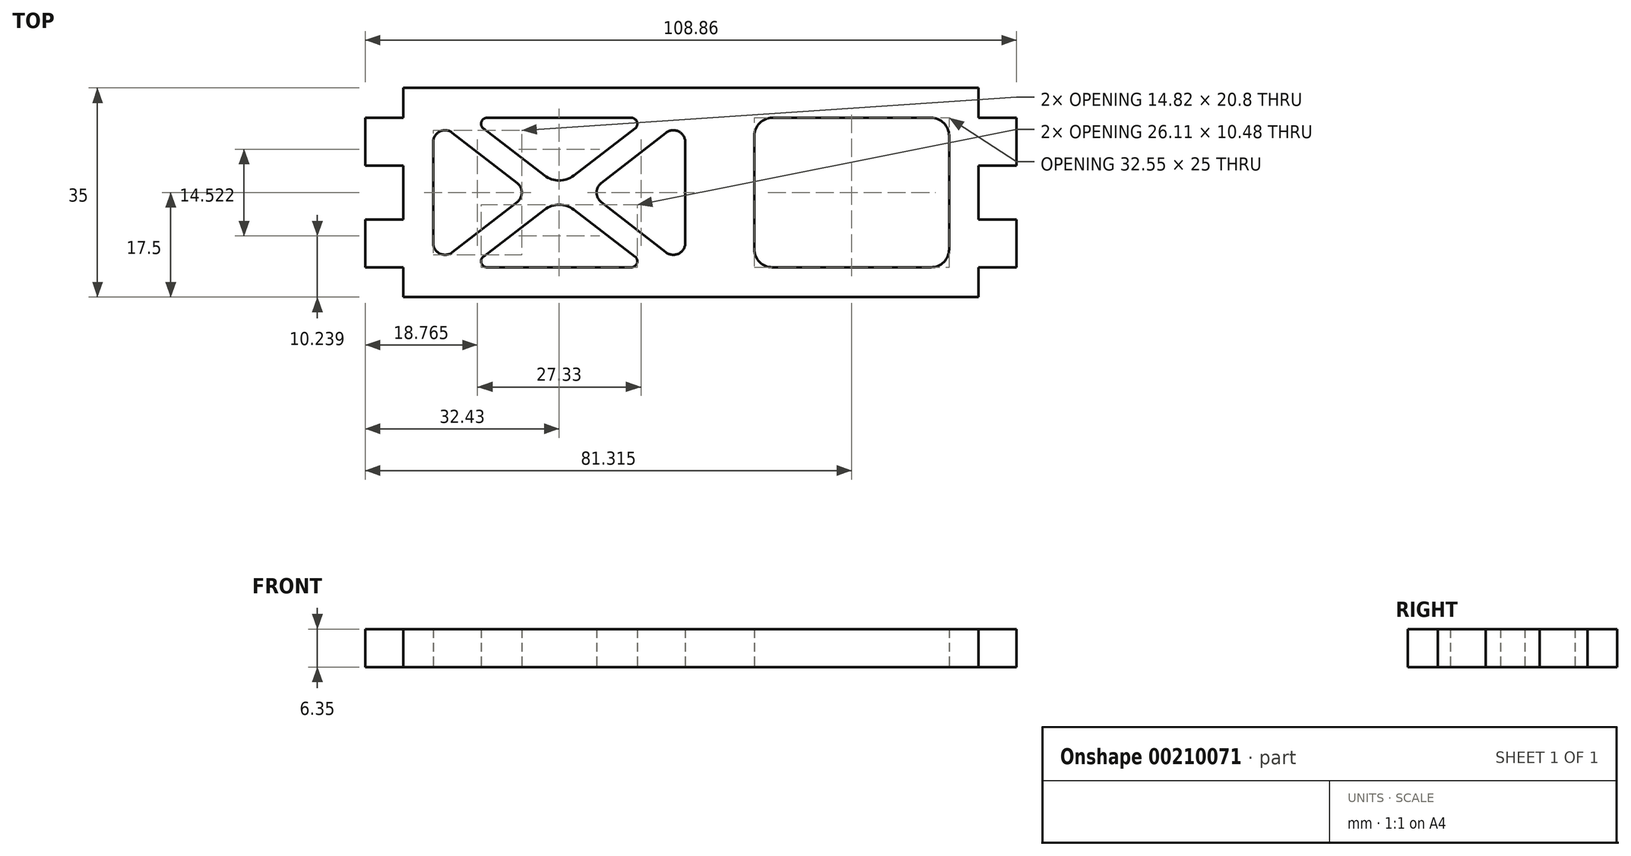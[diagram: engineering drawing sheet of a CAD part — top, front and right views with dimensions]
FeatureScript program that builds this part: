
annotation { "Feature Type Name" : "Feature", "Feature Type Description" : "" }
export const myFeature = defineFeature(function(context is Context, id is Id, definition is map)
    precondition{}
    {
        {
            var Q0;
            Q0=qCreatedBy(makeId("Top.planeOp"),FACE);
            var sketch = newSketch(context, id + "F0", { "sketchPlane" : qUnion([Q0])});
            skLineSegment(sketch, "E0.bottom", {"start": v(-48.08, 17.5) * mm, "end": v(48.08, 17.5) * mm});
            skLineSegment(sketch, "E0.top", {"start": v(-48.08, -17.5) * mm, "end": v(48.08, -17.5) * mm});
            skLineSegment(sketch, "E0.left", {"start": v(-48.08, 17.5) * mm, "end": v(-48.08, -17.5) * mm});
            skLineSegment(sketch, "E0.right", {"start": v(48.08, 17.5) * mm, "end": v(48.08, -17.5) * mm});
            skPoint(sketch, "E0.middle", {"position": v(0, 0) * mm});
            skLineSegment(sketch, "E1.bottom", {"start": v(48.08, 12.5) * mm, "end": v(54.43, 12.5) * mm});
            skLineSegment(sketch, "E1.top", {"start": v(48.08, 4.5) * mm, "end": v(54.43, 4.5) * mm});
            skLineSegment(sketch, "E1.left", {"start": v(48.08, 12.5) * mm, "end": v(48.08, 4.5) * mm});
            skLineSegment(sketch, "E1.right", {"start": v(54.43, 12.5) * mm, "end": v(54.43, 4.5) * mm});
            skLineSegment(sketch, "E2.bottom", {"start": v(48.08, -4.5) * mm, "end": v(54.43, -4.5) * mm});
            skLineSegment(sketch, "E2.top", {"start": v(48.08, -12.5) * mm, "end": v(54.43, -12.5) * mm});
            skLineSegment(sketch, "E2.left", {"start": v(48.08, -4.5) * mm, "end": v(48.08, -12.5) * mm});
            skLineSegment(sketch, "E2.right", {"start": v(54.43, -4.5) * mm, "end": v(54.43, -12.5) * mm});
            skLineSegment(sketch, "E3.bottom", {"start": v(-48.08, 12.5) * mm, "end": v(-54.43, 12.5) * mm});
            skLineSegment(sketch, "E3.top", {"start": v(-48.08, 4.5) * mm, "end": v(-54.43, 4.5) * mm});
            skLineSegment(sketch, "E3.left", {"start": v(-48.08, 12.5) * mm, "end": v(-48.08, 4.5) * mm});
            skLineSegment(sketch, "E3.right", {"start": v(-54.43, 12.5) * mm, "end": v(-54.43, 4.5) * mm});
            skLineSegment(sketch, "E4.bottom", {"start": v(-48.08, -4.5) * mm, "end": v(-54.43, -4.5) * mm});
            skLineSegment(sketch, "E4.top", {"start": v(-48.08, -12.5) * mm, "end": v(-54.43, -12.5) * mm});
            skLineSegment(sketch, "E4.left", {"start": v(-48.08, -4.5) * mm, "end": v(-48.08, -12.5) * mm});
            skLineSegment(sketch, "E4.right", {"start": v(-54.43, -4.5) * mm, "end": v(-54.43, -12.5) * mm});
            skLineSegment(sketch, "E5.bottom", {"start": v(-33.75, -17.5) * mm, "end": v(-22.5, -17.5) * mm});
            skLineSegment(sketch, "E5.top", {"start": v(-33.75, -23.85) * mm, "end": v(-22.5, -23.85) * mm});
            skLineSegment(sketch, "E5.left", {"start": v(-33.75, -17.5) * mm, "end": v(-33.75, -23.85) * mm});
            skLineSegment(sketch, "E5.right", {"start": v(-22.5, -17.5) * mm, "end": v(-22.5, -23.85) * mm});
            skLineSegment(sketch, "E6.bottom", {"start": v(-2.5, -17.5) * mm, "end": v(8.75, -17.5) * mm});
            skLineSegment(sketch, "E6.top", {"start": v(-2.5, -23.85) * mm, "end": v(8.75, -23.85) * mm});
            skLineSegment(sketch, "E6.left", {"start": v(-2.5, -17.5) * mm, "end": v(-2.5, -23.85) * mm});
            skLineSegment(sketch, "E6.right", {"start": v(8.75, -17.5) * mm, "end": v(8.75, -23.85) * mm});
            skLineSegment(sketch, "E7", {"start": v(-48.08, 0) * mm, "end": v(48.08, 0) * mm, "construction": true});
            skLineSegment(sketch, "E8.bottom", {"start": v(40.16, 12.5) * mm, "end": v(13.6, 12.5) * mm});
            skLineSegment(sketch, "E8.top", {"start": v(40.16, -12.5) * mm, "end": v(13.6, -12.5) * mm});
            skLineSegment(sketch, "E8.left", {"start": v(43.16, 9.5) * mm, "end": v(43.16, -9.5) * mm});
            skLineSegment(sketch, "E8.right", {"start": v(10.6, 9.5) * mm, "end": v(10.6, -9.5) * mm});
            skPoint(sketch, "E8.middle", {"position": v(26.89, 0) * mm});
            skPoint(sketch, "E9.visualSharp", {"position": v(10.6, 12.5) * mm});
            skArc(sketch, "E9.filletArc", {"start": v(13.6, 12.5) * mm, "mid": v(11.49, 11.62) * mm, "end": v(10.6, 9.5) * mm});
            skPoint(sketch, "E10.visualSharp", {"position": v(10.6, -12.5) * mm});
            skArc(sketch, "E10.filletArc", {"start": v(10.6, -9.5) * mm, "mid": v(11.49, -11.62) * mm, "end": v(13.6, -12.5) * mm});
            skPoint(sketch, "E11.visualSharp", {"position": v(43.16, -12.5) * mm});
            skArc(sketch, "E11.filletArc", {"start": v(40.16, -12.5) * mm, "mid": v(42.28, -11.62) * mm, "end": v(43.16, -9.5) * mm});
            skPoint(sketch, "E12.visualSharp", {"position": v(43.16, 12.5) * mm});
            skArc(sketch, "E12.filletArc", {"start": v(43.16, 9.5) * mm, "mid": v(42.28, 11.62) * mm, "end": v(40.16, 12.5) * mm});
            skLineSegment(sketch, "E13", {"start": v(-43.08, 0) * mm, "end": v(-43.08, -8.41) * mm});
            skLineSegment(sketch, "E14", {"start": v(-39.85, -10) * mm, "end": v(-29.03, -1.58) * mm});
            skLineSegment(sketch, "E15", {"start": v(-28.26, 0) * mm, "end": v(-28.26, 0) * mm});
            skPoint(sketch, "E16.visualSharp", {"position": v(-43.08, -12.5) * mm});
            skArc(sketch, "E16.filletArc", {"start": v(-43.08, -8.41) * mm, "mid": v(-41.95, -10.2) * mm, "end": v(-39.85, -10) * mm});
            skPoint(sketch, "E17.visualSharp", {"position": v(-28.26, -0.98) * mm});
            skArc(sketch, "E17.filletArc", {"start": v(-29.03, -1.58) * mm, "mid": v(-28.46, -0.88) * mm, "end": v(-28.26, 0) * mm});
            skLineSegment(sketch, "E18", {"start": v(0, 17.5) * mm, "end": v(0, -17.5) * mm, "construction": true});
            skLineSegment(sketch, "E19", {"start": v(-22, 17.5) * mm, "end": v(-22, -17.5) * mm, "construction": true});
            skLineSegment(sketch, "E20.MirrorCS", {"start": v(-15.74, 0) * mm, "end": v(-15.74, 0) * mm});
            skArc(sketch, "E21.MirrorCS", {"start": v(-14.97, -1.58) * mm, "mid": v(-15.54, -0.88) * mm, "end": v(-15.74, 0) * mm});
            skLineSegment(sketch, "E22.MirrorCS", {"start": v(-0.92, 0) * mm, "end": v(-0.92, -8.41) * mm});
            skLineSegment(sketch, "E23.MirrorCS", {"start": v(-4.15, -10) * mm, "end": v(-14.97, -1.58) * mm});
            skArc(sketch, "E24.MirrorCS", {"start": v(-0.92, -8.41) * mm, "mid": v(-2.05, -10.2) * mm, "end": v(-4.15, -10) * mm});
            skLineSegment(sketch, "E25.MirrorCS", {"start": v(-43.08, 0) * mm, "end": v(-43.08, 8.41) * mm});
            skArc(sketch, "E26.MirrorCS", {"start": v(-43.08, 8.41) * mm, "mid": v(-41.95, 10.2) * mm, "end": v(-39.85, 10) * mm});
            skLineSegment(sketch, "E27.MirrorCS", {"start": v(-39.85, 10) * mm, "end": v(-29.03, 1.58) * mm});
            skArc(sketch, "E28.MirrorCS", {"start": v(-29.03, 1.58) * mm, "mid": v(-28.46, 0.88) * mm, "end": v(-28.26, 0) * mm});
            skArc(sketch, "E29.MirrorCS", {"start": v(-14.97, 1.58) * mm, "mid": v(-15.54, 0.88) * mm, "end": v(-15.74, 0) * mm});
            skLineSegment(sketch, "E30.MirrorCS", {"start": v(-0.92, 0) * mm, "end": v(-0.92, 8.41) * mm});
            skLineSegment(sketch, "E31.MirrorCS", {"start": v(-4.15, 10) * mm, "end": v(-14.97, 1.58) * mm});
            skArc(sketch, "E32.MirrorCS", {"start": v(-0.92, 8.41) * mm, "mid": v(-2.05, 10.2) * mm, "end": v(-4.15, 10) * mm});
            skLineSegment(sketch, "E33", {"start": v(-34.67, -10.7) * mm, "end": v(-24.44, -2.85) * mm});
            skLineSegment(sketch, "E34", {"start": v(-19.56, -2.85) * mm, "end": v(-9.33, -10.7) * mm});
            skLineSegment(sketch, "E35", {"start": v(-9.94, -12.5) * mm, "end": v(-34.06, -12.5) * mm});
            skPoint(sketch, "E36.visualSharp", {"position": v(-37, -12.5) * mm});
            skArc(sketch, "E36.filletArc", {"start": v(-34.67, -10.7) * mm, "mid": v(-35, -11.82) * mm, "end": v(-34.06, -12.5) * mm});
            skPoint(sketch, "E37.visualSharp", {"position": v(-7, -12.5) * mm});
            skArc(sketch, "E37.filletArc", {"start": v(-9.94, -12.5) * mm, "mid": v(-9, -11.82) * mm, "end": v(-9.33, -10.7) * mm});
            skPoint(sketch, "E38.visualSharp", {"position": v(-22, -0.98) * mm});
            skArc(sketch, "E38.filletArc", {"start": v(-19.56, -2.85) * mm, "mid": v(-22, -2.02) * mm, "end": v(-24.44, -2.85) * mm});
            skArc(sketch, "E39.MirrorCS", {"start": v(-34.67, 10.7) * mm, "mid": v(-35, 11.82) * mm, "end": v(-34.06, 12.5) * mm});
            skLineSegment(sketch, "E40.MirrorCS", {"start": v(-9.94, 12.5) * mm, "end": v(-34.06, 12.5) * mm});
            skArc(sketch, "E41.MirrorCS", {"start": v(-9.94, 12.5) * mm, "mid": v(-9, 11.82) * mm, "end": v(-9.33, 10.7) * mm});
            skLineSegment(sketch, "E42.MirrorCS", {"start": v(-34.67, 10.7) * mm, "end": v(-24.44, 2.85) * mm});
            skLineSegment(sketch, "E43.MirrorCS", {"start": v(-19.56, 2.85) * mm, "end": v(-9.33, 10.7) * mm});
            skArc(sketch, "E44.MirrorCS", {"start": v(-19.56, 2.85) * mm, "mid": v(-22, 2.02) * mm, "end": v(-24.44, 2.85) * mm});
            skSolve(sketch);
        }
        {
            var Q0;
            {var subQ1=sQuery(id+"F0.wireOp",EDGE,"E0.bottom");Q0=makeQuery(id+"F0.imprint","IMPRINT",FACE,{"disambiguationData":[TD([[makeQuery(id+"F0.imprint","IMPRINT",EDGE,{"derivedFrom":subQ1}),-1.0]])]});}
            var Q1;
            Q1=makeQuery(id+"F0.imprint","IMPRINT",FACE,{"disambiguationData":[TD([[makeQuery(id+"F0.imprint","IMPRINT",EDGE,{"derivedFrom":sQuery(id+"F0.wireOp",EDGE,"E3.bottom")}),1.0]])]});
            var Q2;
            Q2=makeQuery(id+"F0.imprint","IMPRINT",FACE,{"disambiguationData":[TD([[makeQuery(id+"F0.imprint","IMPRINT",EDGE,{"derivedFrom":sQuery(id+"F0.wireOp",EDGE,"E4.bottom")}),1.0]])]});
            var Q3;
            Q3=makeQuery(id+"F0.imprint","IMPRINT",FACE,{"disambiguationData":[TD([[makeQuery(id+"F0.imprint","IMPRINT",EDGE,{"derivedFrom":sQuery(id+"F0.wireOp",EDGE,"E5.bottom")}),-1.0]])]});
            var Q4;
            Q4=makeQuery(id+"F0.imprint","IMPRINT",FACE,{"disambiguationData":[TD([[makeQuery(id+"F0.imprint","IMPRINT",EDGE,{"derivedFrom":sQuery(id+"F0.wireOp",EDGE,"E6.bottom")}),-1.0]])]});
            var Q5;
            Q5=makeQuery(id+"F0.imprint","IMPRINT",FACE,{"disambiguationData":[TD([[makeQuery(id+"F0.imprint","IMPRINT",EDGE,{"derivedFrom":sQuery(id+"F0.wireOp",EDGE,"E2.bottom")}),-1.0]])]});
            var Q6;
            Q6=makeQuery(id+"F0.imprint","IMPRINT",FACE,{"disambiguationData":[TD([[makeQuery(id+"F0.imprint","IMPRINT",EDGE,{"derivedFrom":sQuery(id+"F0.wireOp",EDGE,"E1.bottom")}),-1.0]])]});
            extrude(context, id + "F1", {"entities" : qUnion([Q0, Q1, Q2, Q3, Q4, Q5, Q6]), "depth" : 6.35 * mm});
        }
    });
